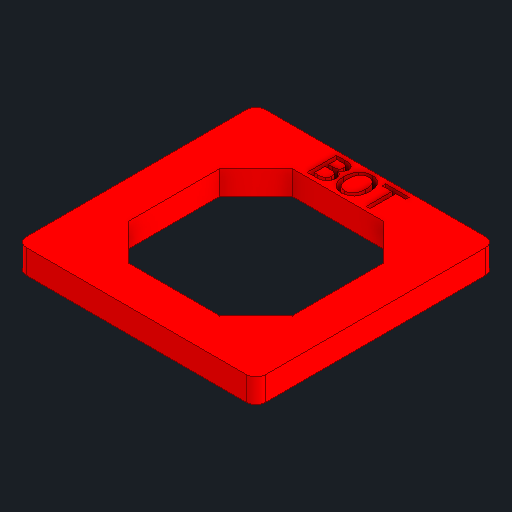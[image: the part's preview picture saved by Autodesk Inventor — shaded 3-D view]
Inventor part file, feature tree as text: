
AUTODESK INVENTOR PART (.ipt)
format: ipt  version: 2023.4 (Build 274418000, 418)  size: 495,616 bytes
history: native  units: mm
features: extrude x9, projected_geometry x9, chamfer x3, fillet x1, pattern_circular x1, sketch x1
ambient origin geometry x8: Origin, YZ Plane, XZ Plane, XY Plane, X Axis, Y Axis, Z Axis, Center Point
bodies: Solid1 (feature_tree)
feature tree (24):
  extrude  "Extrusion1"  Depth=49.8mm
  extrude  "Extrusion2"  Depth=7.85mm
  chamfer  "Chamfer1"  Distance=3.0mm
  fillet  "Fillet1"  Radius=3.0mm
  chamfer  "Chamfer2"  Distance=3.75mm
  extrude  "Extrusion3"  Depth=4.2125mm
  extrude  "Extrusion4"  Depth=0.675mm
  extrude  "Extrusion5"  Depth=10.5mm
  pattern_circular  "Circular Pattern1"  [2 undecoded]
  extrude  "Extrusion6"  Depth=4.1mm
  extrude  "Extrusion7"  Depth=4.145mm
  chamfer  "Chamfer3"  Distance=7.85mm
  extrude  "Extrusion8"  Depth=7.85mm
  extrude  "Extrusion9"  Depth=5.5mm
  sketch  "Sketch2"  dims[d0=49.8mm d1=49.8mm d2=7.85mm d3=3.0mm d4=3.0mm d5=3.75mm d6=4.2125mm d7=0.675mm d8=10.5mm d9=10.5mm d10=4.1mm d11=4.145mm d12=7.85mm d13=7.85mm d14=5.5mm d15=5.5mm d16=40.0mm d18=360.0deg d20=7.7mm d21=0.0mm d22=2.2mm d23=0.0mm d24=5.5mm d25=2.0mm d26=45.0deg d27=2.0mm d28=0.025mm d29=2.0mm d30=45.0deg d31=3.0mm d32=0.0mm d33=3.0mm d34=0.0mm d35=0.75mm d36=0.0mm d37=40.0mm d38=360.0deg d40=2.2mm d41=0.0mm d42=5.7mm d43=0.0mm d44=7.5mm d45=2.0mm d46=45.0deg d47=2.7mm d48=0.0mm d49=20.0mm d50=2.5mm d51=0.0mm]
  projected_geometry  "Projected Loop2"
  projected_geometry  "Projected Loop3"
  projected_geometry  "Projected Loop4"
  projected_geometry  "Projected Loop5"
  projected_geometry  "Projected Loop6"
  projected_geometry  "Projected Loop7"
  projected_geometry  "Projected Loop8"
  projected_geometry  "Projected Loop9"
  projected_geometry  "Projected Loop10"
note: 2 required parameter values undecoded (feature->parameter linkage not recoverable at this tier; creation-order binding heuristic only, values carry confidence <= 0.55)
